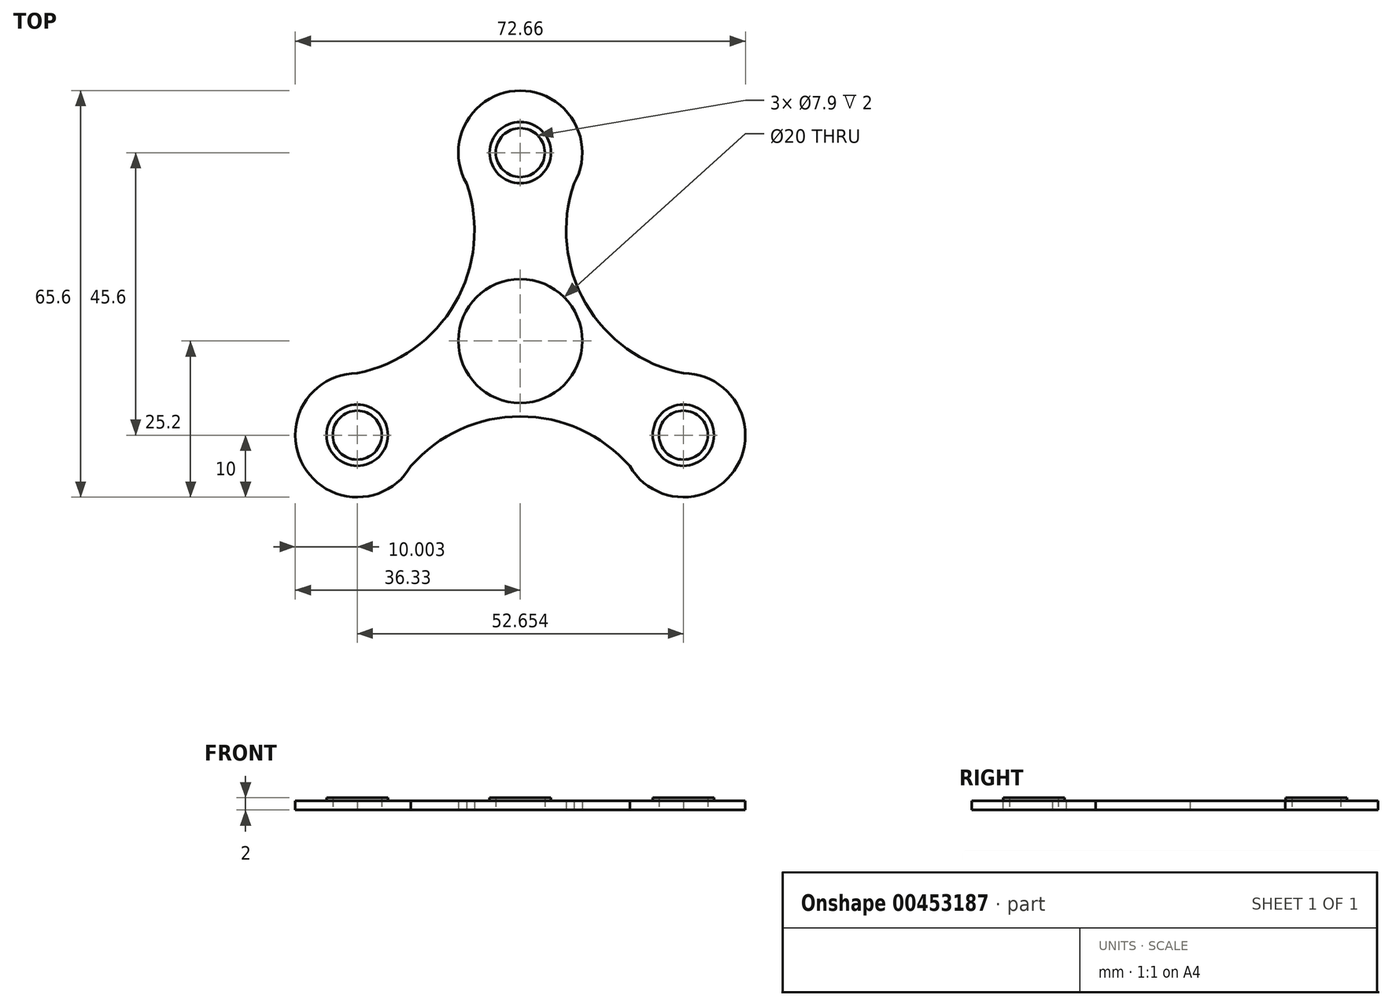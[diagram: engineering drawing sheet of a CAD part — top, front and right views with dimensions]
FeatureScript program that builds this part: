
annotation { "Feature Type Name" : "Feature", "Feature Type Description" : "" }
export const myFeature = defineFeature(function(context is Context, id is Id, definition is map)
    precondition{}
    {
        {
            var Q0;
            Q0=qCreatedBy(makeId("Top.planeOp"),FACE);
            var sketch = newSketch(context, id + "F0", { "sketchPlane" : qUnion([Q0])});
            skCircle(sketch, "E0", {"center": v(0, 0) * mm, "radius": 10 * mm});
            skCircle(sketch, "E1", {"center": v(0, 30.4) * mm, "radius": 3.95 * mm});
            skCircle(sketch, "E2.0", {"center": v(0, 30.4) * mm, "radius": 4.95 * mm});
            skCircle(sketch, "E3", {"center": v(0, 30.4) * mm, "radius": 10 * mm});
            skLineSegment(sketch, "E4", {"start": v(0, 30.4) * mm, "end": v(-8.66, 25.4) * mm});
            skLineSegment(sketch, "E5.MirrorCS", {"start": v(0, 30.4) * mm, "end": v(8.66, 25.4) * mm});
            skLineSegment(sketch, "E6.1.0", {"start": v(-26.33, -15.2) * mm, "end": v(-17.67, -20.2) * mm});
            skCircle(sketch, "E6.1.1", {"center": v(-26.33, -15.2) * mm, "radius": 10 * mm});
            skCircle(sketch, "E6.1.2", {"center": v(-26.33, -15.2) * mm, "radius": 4.95 * mm});
            skCircle(sketch, "E6.1.3", {"center": v(-26.33, -15.2) * mm, "radius": 3.95 * mm});
            skLineSegment(sketch, "E6.1.4", {"start": v(-26.33, -15.2) * mm, "end": v(-26.33, -5.2) * mm});
            skLineSegment(sketch, "E6.2.0", {"start": v(26.33, -15.2) * mm, "end": v(26.33, -5.2) * mm});
            skCircle(sketch, "E6.2.1", {"center": v(26.33, -15.2) * mm, "radius": 10 * mm});
            skCircle(sketch, "E6.2.2", {"center": v(26.33, -15.2) * mm, "radius": 4.95 * mm});
            skCircle(sketch, "E6.2.3", {"center": v(26.33, -15.2) * mm, "radius": 3.95 * mm});
            skLineSegment(sketch, "E6.2.4", {"start": v(26.33, -15.2) * mm, "end": v(17.67, -20.2) * mm});
            skArc(sketch, "E7", {"start": v(-26.33, -5.2) * mm, "mid": v(-10.55, 6.1) * mm, "end": v(-8.66, 25.4) * mm});
            skArc(sketch, "E8.1.0", {"start": v(17.67, -20.2) * mm, "mid": v(0, -12.18) * mm, "end": v(-17.67, -20.2) * mm});
            skArc(sketch, "E8.2.0", {"start": v(8.66, 25.4) * mm, "mid": v(10.55, 6.09) * mm, "end": v(26.33, -5.2) * mm});
            skSolve(sketch);
        }
        {
            var Q0;
            Q0=makeQuery(id+"F0.imprint","IMPRINT",FACE,{"disambiguationData":[TD([[makeQuery(id+"F0.imprint","IMPRINT",EDGE,{"derivedFrom":sQuery(id+"F0.wireOp",EDGE,"E0")}),-1.0]])]});
            var Q1;
            {var subQ0=sQuery(id+"F0.wireOp",EDGE,"E4");var subQ1=sQuery(id+"F0.wireOp",EDGE,"E2.0");var subQ2=makeQuery(id+"F0.imprint","INTERSECT",VERTEX,{"derivedFrom":[subQ1,subQ0]});Q1=makeQuery(id+"F0.imprint","IMPRINT",FACE,{"disambiguationData":[TD([[makeQuery(id+"F0.imprint","IMPRINT",EDGE,{"disambiguationData":[TD([[subQ2,-1.0]])],"derivedFrom":subQ1}),-1.0]])]});}
            var Q2;
            {var subQ0=sQuery(id+"F0.wireOp",EDGE,"E4");var subQ1=sQuery(id+"F0.wireOp",EDGE,"E2.0");var subQ2=makeQuery(id+"F0.imprint","INTERSECT",VERTEX,{"derivedFrom":[subQ1,subQ0]});Q2=makeQuery(id+"F0.imprint","IMPRINT",FACE,{"disambiguationData":[TD([[makeQuery(id+"F0.imprint","IMPRINT",EDGE,{"disambiguationData":[TD([[subQ2,1.0]])],"derivedFrom":subQ1}),-1.0]])]});}
            var Q3;
            {var subQ1=sQuery(id+"F0.wireOp",EDGE,"E6.2.0");var subQ3=sQuery(id+"F0.wireOp",EDGE,"E6.2.2");var subQ4=makeQuery(id+"F0.imprint","INTERSECT",VERTEX,{"derivedFrom":[subQ1,subQ3]});Q3=makeQuery(id+"F0.imprint","IMPRINT",FACE,{"disambiguationData":[TD([[makeQuery(id+"F0.imprint","IMPRINT",EDGE,{"disambiguationData":[TD([[subQ4,-1.0]])],"derivedFrom":subQ3}),-1.0]])]});}
            var Q4;
            {var subQ1=sQuery(id+"F0.wireOp",EDGE,"E6.2.0");var subQ3=sQuery(id+"F0.wireOp",EDGE,"E6.2.2");var subQ4=makeQuery(id+"F0.imprint","INTERSECT",VERTEX,{"derivedFrom":[subQ1,subQ3]});Q4=makeQuery(id+"F0.imprint","IMPRINT",FACE,{"disambiguationData":[TD([[makeQuery(id+"F0.imprint","IMPRINT",EDGE,{"disambiguationData":[TD([[subQ4,1.0]])],"derivedFrom":subQ3}),-1.0]])]});}
            var Q5;
            {var subQ1=sQuery(id+"F0.wireOp",EDGE,"E6.1.0");var subQ3=sQuery(id+"F0.wireOp",EDGE,"E6.1.2");var subQ4=makeQuery(id+"F0.imprint","INTERSECT",VERTEX,{"derivedFrom":[subQ1,subQ3]});Q5=makeQuery(id+"F0.imprint","IMPRINT",FACE,{"disambiguationData":[TD([[makeQuery(id+"F0.imprint","IMPRINT",EDGE,{"disambiguationData":[TD([[subQ4,-1.0]])],"derivedFrom":subQ3}),-1.0]])]});}
            var Q6;
            {var subQ1=sQuery(id+"F0.wireOp",EDGE,"E6.1.0");var subQ3=sQuery(id+"F0.wireOp",EDGE,"E6.1.2");var subQ4=makeQuery(id+"F0.imprint","INTERSECT",VERTEX,{"derivedFrom":[subQ1,subQ3]});Q6=makeQuery(id+"F0.imprint","IMPRINT",FACE,{"disambiguationData":[TD([[makeQuery(id+"F0.imprint","IMPRINT",EDGE,{"disambiguationData":[TD([[subQ4,1.0]])],"derivedFrom":subQ3}),-1.0]])]});}
            extrude(context, id + "F1", {"entities" : qUnion([Q0, Q1, Q2, Q3, Q4, Q5, Q6]), "depth" : 1.5 * mm});
        }
        {
            var Q0;
            {var subQ0=sQuery(id+"F0.wireOp",EDGE,"E4");var subQ1=sQuery(id+"F0.wireOp",EDGE,"E1");var subQ2=makeQuery(id+"F0.imprint","INTERSECT",VERTEX,{"derivedFrom":[subQ1,subQ0]});Q0=makeQuery(id+"F0.imprint","IMPRINT",FACE,{"disambiguationData":[TD([[makeQuery(id+"F0.imprint","IMPRINT",EDGE,{"disambiguationData":[TD([[subQ2,-1.0]])],"derivedFrom":subQ1}),-1.0]])]});}
            var Q1;
            {var subQ0=sQuery(id+"F0.wireOp",EDGE,"E4");var subQ1=sQuery(id+"F0.wireOp",EDGE,"E1");var subQ2=makeQuery(id+"F0.imprint","INTERSECT",VERTEX,{"derivedFrom":[subQ1,subQ0]});Q1=makeQuery(id+"F0.imprint","IMPRINT",FACE,{"disambiguationData":[TD([[makeQuery(id+"F0.imprint","IMPRINT",EDGE,{"disambiguationData":[TD([[subQ2,1.0]])],"derivedFrom":subQ1}),-1.0]])]});}
            var Q2;
            {var subQ0=sQuery(id+"F0.wireOp",EDGE,"E6.2.3");var subQ1=sQuery(id+"F0.wireOp",EDGE,"E6.2.0");var subQ2=makeQuery(id+"F0.imprint","INTERSECT",VERTEX,{"derivedFrom":[subQ1,subQ0]});Q2=makeQuery(id+"F0.imprint","IMPRINT",FACE,{"disambiguationData":[TD([[makeQuery(id+"F0.imprint","IMPRINT",EDGE,{"disambiguationData":[TD([[subQ2,-1.0]])],"derivedFrom":subQ1}),1.0]])]});}
            var Q3;
            {var subQ0=sQuery(id+"F0.wireOp",EDGE,"E6.2.3");var subQ1=sQuery(id+"F0.wireOp",EDGE,"E6.2.0");var subQ2=makeQuery(id+"F0.imprint","INTERSECT",VERTEX,{"derivedFrom":[subQ1,subQ0]});Q3=makeQuery(id+"F0.imprint","IMPRINT",FACE,{"disambiguationData":[TD([[makeQuery(id+"F0.imprint","IMPRINT",EDGE,{"disambiguationData":[TD([[subQ2,-1.0]])],"derivedFrom":subQ1}),-1.0]])]});}
            var Q4;
            {var subQ0=sQuery(id+"F0.wireOp",EDGE,"E6.1.3");var subQ1=sQuery(id+"F0.wireOp",EDGE,"E6.1.0");var subQ2=makeQuery(id+"F0.imprint","INTERSECT",VERTEX,{"derivedFrom":[subQ1,subQ0]});Q4=makeQuery(id+"F0.imprint","IMPRINT",FACE,{"disambiguationData":[TD([[makeQuery(id+"F0.imprint","IMPRINT",EDGE,{"disambiguationData":[TD([[subQ2,-1.0]])],"derivedFrom":subQ1}),1.0]])]});}
            var Q5;
            {var subQ0=sQuery(id+"F0.wireOp",EDGE,"E6.1.3");var subQ1=sQuery(id+"F0.wireOp",EDGE,"E6.1.0");var subQ2=makeQuery(id+"F0.imprint","INTERSECT",VERTEX,{"derivedFrom":[subQ1,subQ0]});Q5=makeQuery(id+"F0.imprint","IMPRINT",FACE,{"disambiguationData":[TD([[makeQuery(id+"F0.imprint","IMPRINT",EDGE,{"disambiguationData":[TD([[subQ2,-1.0]])],"derivedFrom":subQ1}),-1.0]])]});}
            extrude(context, id + "F2", {"entities" : qUnion([Q0, Q1, Q2, Q3, Q4, Q5]), "operationType" : NewBodyOperationType.ADD, "depth" : 2 * mm});
        }
    });
